# Revit family: ST6000001 Dispensador De Jabon Orvallo
name_source: partatom
category: Aparatos sanitarios
revit_build: Autodesk Revit 2018 (Build: 20170223_1515(x64)
units: mm (PartAtom-declared; Revit-internal decimal feet)

## family parameters
Anfitrión = Cara
Compartido = No
Corte con vacíos al cargar = No
Cota de conector redondo = Diámetro de uso
Número OmniClass = 23.45.05.00
Punto de cálculo de habitación = No
Tipo de pieza = Normal
Título OmniClass = Sanitary Equipment

## types (1)
- ST6000001 Dispensador De Jabon Orvallo
    Accionamiento = Sensor
    Capacidad de descarga = Descarga de 0,8 CC
    Conexión = Entrada de 110 VAC y Salida a 9VDC
    Código de montaje = D2010
    Elevación por defecto = 1219 mm
    Garantía = 2 años
    Marca = CORONA
    Material = <Por categoría>
    Material Acabado = Cromo
    Material de fabricación = Latón y componentes poliméricos
    Nombre = Dispensador De Jabón Orvallo
    Presión mínima = Viscosidad REQUERIDA 100 - 3800 mm.
    Referencia = ST6000001
    Tipo = Accesorio
    Tráfico = Institucional, alto tráfico
    URL = https://www.corona.co
    Vida util ( ciclos ) = 150.000
